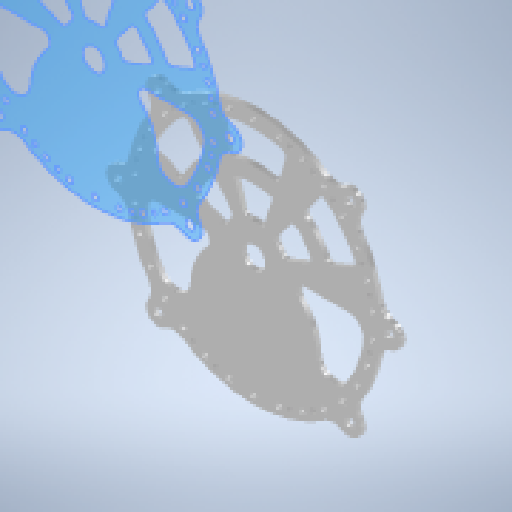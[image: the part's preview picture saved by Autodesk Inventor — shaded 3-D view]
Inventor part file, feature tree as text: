
AUTODESK INVENTOR PART (.ipt)
format: ipt  version: 2024 (Build 280153000, 153)  size: 434,688 bytes
history: native  units: mm
features: thread x16, sketch x8, extrude x4, hole x4, pattern_circular x2, other x1, fillet x1
ambient origin geometry x8: Origin, YZ Plane, XZ Plane, XY Plane, X Axis, Y Axis, Z Axis, Center Point
bodies: Body1 (feature_tree)
feature tree (36):
  other  "ソリッド1"
  extrude  "押し出し1"  Depth=160.0mm
  hole  "穴1"  [1 undecoded]
  pattern_circular  "円形状パターン1"  Count=15  [1 undecoded]
  hole  "穴2"  [1 undecoded]
  hole  "穴3"  [1 undecoded]
  thread  "ねじ1"
  thread  "ねじ2"
  thread  "ねじ3"
  thread  "ねじ4"
  thread  "ねじ5"
  thread  "ねじ6"
  thread  "ねじ7"
  thread  "ねじ8"
  thread  "ねじ9"
  thread  "ねじ10"
  thread  "ねじ11"
  thread  "ねじ12"
  thread  "ねじ13"
  thread  "ねじ14"
  thread  "ねじ15"
  thread  "ねじ16"
  extrude  "押し出し2"  Depth=150.0mm
  hole  "穴4"  [1 undecoded]
  pattern_circular  "円形状パターン2"  Count=6 Angle=60.0deg
  extrude  "押し出し3"  Depth=3.0mm TaperAngle=0.0deg
  extrude  "押し出し4"  Depth=3.0mm TaperAngle=0.0deg
  fillet  "フィレット1"  Radius=3.0mm
  sketch  "スケッチ1"
  sketch  "スケッチ2"
  sketch  "スケッチ3"
  sketch  "スケッチ4"
  sketch  "スケッチ5"
  sketch  "スケッチ6"
  sketch  "スケッチ7"
  sketch  "スケッチ8"
note: 5 required parameter values undecoded (feature->parameter linkage not recoverable at this tier; creation-order binding heuristic only, values carry confidence <= 0.55)
